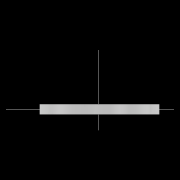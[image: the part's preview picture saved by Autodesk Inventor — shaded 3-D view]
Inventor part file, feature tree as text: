
AUTODESK INVENTOR PART (.ipt)
format: ipt  version: 2022.2 (Build 262287010, 287A)  size: 894,976 bytes
history: native  units: mm
features: extrude x19, sketch x18, pattern_circular x15, other x14, revolve x7, hole x7, move_body x4, fillet x2, draft x2
ambient origin geometry x8: Origin, YZ Plane, XZ Plane, XY Plane, X Axis, Y Axis, Z Axis, Center Point
bodies: Solid1 (feature_tree), Solid2 (feature_tree), Solid3 (feature_tree), Solid4 (feature_tree), Solid5 (feature_tree)
feature tree (88):
  sketch  "Sketch7"  dims[d21=0.5mm]
  other  "Roller1"
  other  "Roller2"
  sketch  "Sketch22"  dims[d39=0.05mm]
  sketch  "Sketch2"  dims[d17=0.05mm]
  sketch  "Sketch23"  dims[d41=0.05mm]
  other  "RevRoller1"
  fillet  "Fillet1"  Radius=0.05mm
  pattern_circular  "Circular Pattern13"  Count=6  [1 undecoded]
  move_body  "Move Body7"
  revolve  "Revolution13"  Angle=30.0deg
  fillet  "Fillet3"  [1 undecoded]
  pattern_circular  "Circular Pattern14"  [2 undecoded]
  move_body  "Move Body6"
  revolve  "Revolution14"  [1 undecoded]
  other  "OuterRim_Top2"
  other  "OuterRim_Bottom2"
  extrude  "Extrusion9"  TaperAngle=90.0deg  [1 undecoded]
  sketch  "Sketch24"  dims[d42=0.5mm]
  extrude  "Extrusion10"  Depth=3.0mm
  extrude  "Extrusion11"  Depth=3.0mm
  pattern_circular  "Circular Pattern15"  [2 undecoded]
  sketch  "Sketch25"  dims[d43=0.5mm]
  extrude  "Extrusion12"  Depth=3.0mm
  extrude  "Extrusion14"  Depth=3.0mm
  extrude  "Extrusion15"  Depth=3.0mm
  pattern_circular  "Circular Pattern16"  [2 undecoded]
  extrude  "Extrusion16"  Depth=3.0mm
  extrude  "Extrusion17"  Depth=3.0mm
  hole  "Hole9"  [1 undecoded]
  pattern_circular  "Circular Pattern17"  [2 undecoded]
  sketch  "Sketch27"  dims[d45=0.5mm]
  hole  "Hole10"  [1 undecoded]
  hole  "Hole11"  [1 undecoded]
  pattern_circular  "Circular Pattern18"  [2 undecoded]
  extrude  "Extrusion18"  Depth=3.0mm
  extrude  "Extrusion19"  Depth=3.0mm
  pattern_circular  "Circular Pattern19"  [2 undecoded]
  sketch  "Sketch28"  dims[d46=0.5mm d47=0.5mm d48=2.0mm d50=90.0deg d56=14.029612mm d57=4.025mm d90=16.473921mm d107=0.05mm d108=0.05mm d109=0.05mm d110=0.05mm d112=0.5mm d113=0.5mm d114=0.5mm d115=14.644822mm d116=14.607374mm d117=1.0mm d118=0.05mm d119=0.05mm d120=0.05mm d121=0.05mm d122=0.5mm d123=0.5mm d124=14.644822mm d125=14.607374mm d126=1.0mm d127=90.0deg d128=30.0deg d129=90.0deg d167=8.972256mm d173=10.814812mm d201=53.5mm d202=90.0deg d203=90.0deg d204=90.0deg d218=53.5mm d226=5.4mm d232=0.0mm d233=3600.0mm d234=10.502mm d235=0.0mm d243=1.902mm d244=0.0mm d246=2.75mm d247=5.251mm d248=0.0mm d249=3.0mm d250=0.0mm d251=90.0mm d252=360.0deg d254=2.75mm d255=3.0mm d256=5.251mm d257=0.0mm d258=3.0mm d259=0.0mm d260=90.0mm d261=360.0deg d277=76.5mm d281=73.5mm d282=24.65mm d283=6.0mm d284=4.0mm d285=2.0mm d286=90.0deg d287=5.251mm d288=0.0mm d289=60.0mm d290=360.0deg d292=0.436332mm d293=60.0mm d294=90.0mm d295=3.0mm d296=6.0mm d297=5.5mm d298=3.0mm d299=90.0deg d300=5.251mm d301=0.0mm d302=60.0mm d303=360.0deg d305=30.0deg d306=73.5mm d307=24.65mm d308=6.0mm d309=5.5mm d310=3.0mm d311=90.0deg d312=5.251mm d313=0.0mm d314=60.0mm d315=360.0deg d317=90.0mm d318=60.0mm d319=30.0deg d320=5.4mm d321=5.4mm d322=3.0mm d323=6.0mm d324=5.5mm d325=3.0mm d326=90.0deg d327=5.251mm d328=0.0mm d329=2.4mm d330=0.0mm d331=60.0mm d332=360.0deg d343=17.307186mm d344=17.309884mm d345=0.025mm d346=0.025mm d347=0.1mm d348=0.1mm d349=17.309884mm d350=17.307186mm d351=0.025mm d352=0.025mm d354=0.1mm d355=17.307186mm d356=17.309884mm d357=1.0mm d358=90.0deg d359=0.5mm d360=60.0mm d361=360.0deg d363=30.0deg d367=8.1mm d369=4.014775mm d370=0.1mm d371=1.0mm d372=30.0deg d373=90.0deg d374=0.5mm d375=60.0mm d376=360.0deg d378=90.0deg d379=0.1mm d380=0.1mm d381=0.1mm d382=0.1mm d383=0.1mm d384=10.502mm d385=0.0mm d386=0.0mm d391=1.0mm d392=53.5mm d393=1.5mm d394=1.5mm d395=1.5mm d396=1.5mm d397=90.0deg d398=90.0deg d399=90.0deg d400=53.5mm d401=10.502mm d402=0.0mm d403=2.75mm d404=1.5mm d405=10.502mm d406=0.0mm d407=3.0mm d408=0.0mm d409=90.0mm d410=360.0deg d412=5.4mm d413=5.251mm d414=0.0mm d417=5.4mm d418=2.4mm d419=0.0mm d420=2.4mm d421=0.0mm d422=90.0mm d423=360.0deg d425=60.0mm d426=90.0mm d427=1.5mm d428=1.5mm d429=5.4mm d430=5.4mm d431=5.251mm d432=0.0mm d433=2.4mm d434=0.0mm d435=30.0deg d436=73.5mm d437=24.65mm d438=6.0mm d439=4.0mm d440=2.0mm d441=90.0deg d442=5.251mm d443=0.0mm d444=60.0mm d445=360.0deg d447=3.0mm d448=6.0mm d449=5.5mm d450=3.0mm d451=90.0deg d452=5.251mm d453=0.0mm d454=24.65mm d455=6.0mm d456=5.5mm d457=3.0mm d458=90.0deg d459=5.251mm d460=0.0mm d461=60.0mm d462=360.0deg d464=5.251mm d465=0.0mm d466=3.0mm d467=0.0mm d468=90.0mm d469=360.0deg d472=1.5mm d474=5.251mm d475=0.0mm d481=3.0mm d482=0.0mm d483=90.0mm d484=360.0deg d486=0.436332mm d49=0.872665mm d51=0.872665mm d52=0.872665mm d236=0.5mm d237=0.872665mm d238=0.5mm d239=0.872665mm d291=0.0625mm d415=0.5mm d416=0.872665mm d471=0.5mm d473=0.5mm]
  extrude  "Extrusion20"  Depth=3.0mm
  extrude  "Extrusion22"  Depth=3.0mm
  pattern_circular  "Circular Pattern21"  [2 undecoded]
  draft  "FaceDraft2"
  other  "InnerRim"
  other  "OuterRim_Top"
  other  "OuterRim_Bottom"
  extrude  "Extrusion2"  Depth=3.0mm
  sketch  "Sketch13"  dims[d24=0.5mm]
  extrude  "Extrusion3"  Depth=1.0mm
  sketch  "Sketch15"  dims[d29=360.0deg d30=60.0mm]
  extrude  "Extrusion4"  TaperAngle=90.0deg  [1 undecoded]
  extrude  "Extrusion5"  TaperAngle=30.0deg  [1 undecoded]
  pattern_circular  "Circular Pattern6"  Angle=90.0deg  [1 undecoded]
  sketch  "Sketch16"  dims[d31=360.0deg d35=30.0deg d36=90.0deg]
  extrude  "Extrusion6"  Depth=3.0mm
  extrude  "Extrusion7"  Depth=3.0mm
  pattern_circular  "Circular Pattern7"  [2 undecoded]
  hole  "Hole5"  [1 undecoded]
  pattern_circular  "Circular Pattern9"  Angle=90.0deg  [1 undecoded]
  draft  "FaceDraft1"
  hole  "Hole6"  [1 undecoded]
  pattern_circular  "Circular Pattern10"  [2 undecoded]
  hole  "Hole7"  [1 undecoded]
  pattern_circular  "Circular Pattern11"  Count=360  [1 undecoded]
  hole  "Hole8"  [1 undecoded]
  extrude  "Extrusion8"  TaperAngle=0.0deg  [1 undecoded]
  pattern_circular  "Circular Pattern12"  [2 undecoded]
  sketch  "Sketch8"  dims[d22=0.5mm]
  sketch  "Sketch9"  dims[d23=0.5mm]
  revolve  "Revolution4"  [1 undecoded]
  move_body  "Move Body4"
  revolve  "Revolution5"  [1 undecoded]
  sketch  "Sketch5"  dims[d19=0.5mm]
  sketch  "Sketch6"  dims[d20=0.5mm]
  revolve  "Revolution3"  [1 undecoded]
  sketch  "Sketch4"  dims[d18=0.05mm]
  revolve  "Revolution1"  [1 undecoded]
  pattern_circular  "Circular Pattern1"  [2 undecoded]
  move_body  "Move Body3"
  revolve  "Revolution2"  [1 undecoded]
  other  "2D Equation Curve1"
  sketch  "Sketch14"  dims[d28=2.0mm]
  other  "Work Axis1"
  other  "Work Axis2"
  other  "Work Axis3"
  other  "Work Axis4"
  other  "Work Axis5"
  sketch  "Sketch26"  dims[d44=0.5mm]
note: 44 required parameter values undecoded (feature->parameter linkage not recoverable at this tier; creation-order binding heuristic only, values carry confidence <= 0.55)